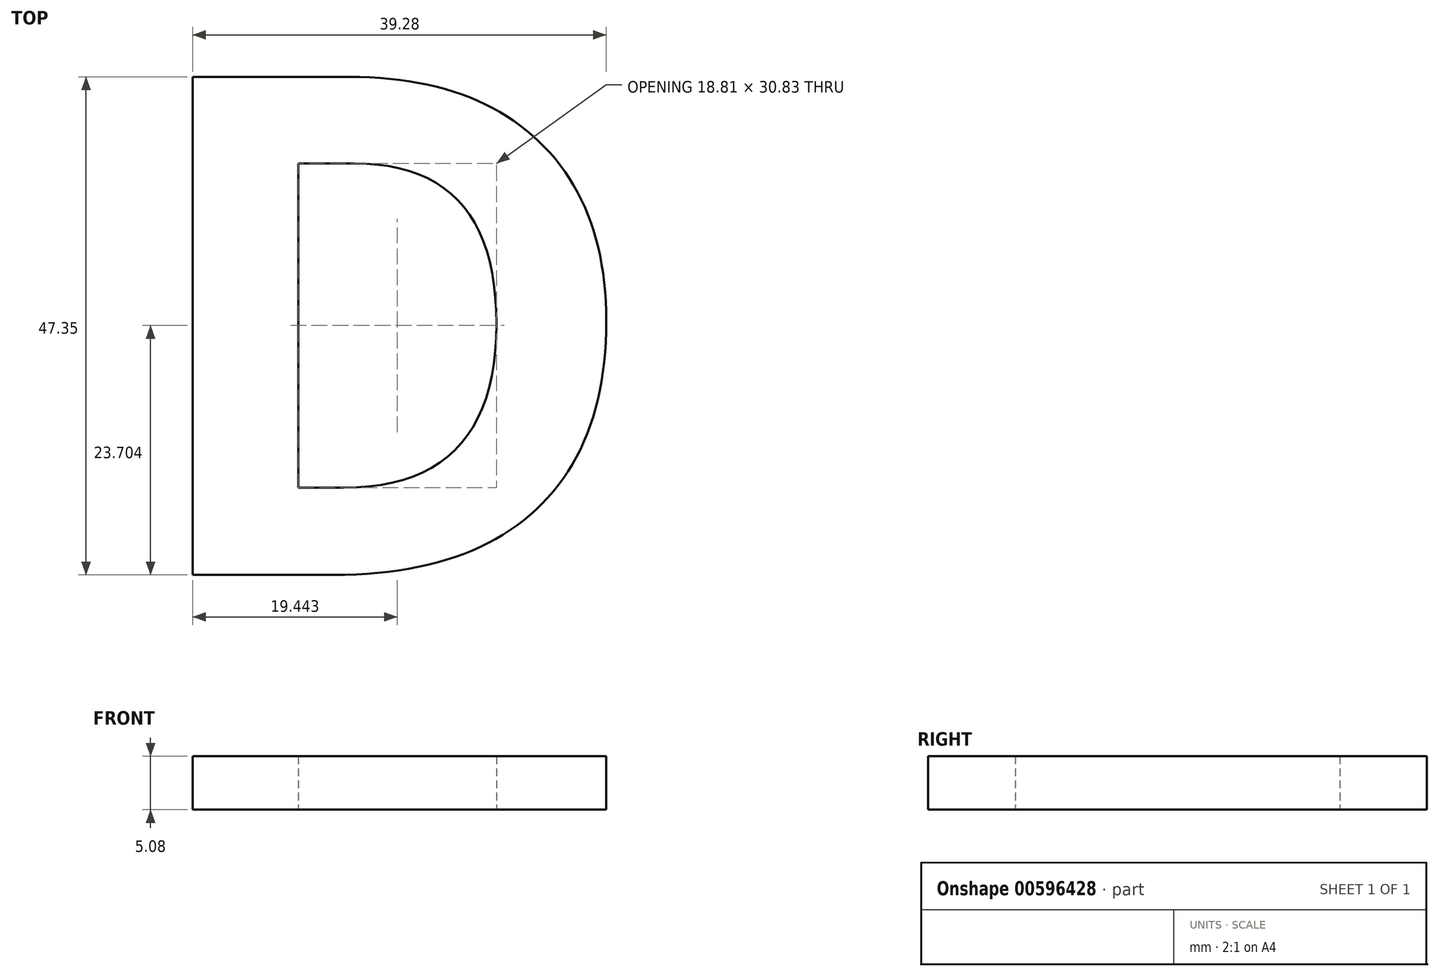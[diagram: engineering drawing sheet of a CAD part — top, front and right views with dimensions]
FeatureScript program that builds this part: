
annotation { "Feature Type Name" : "Feature", "Feature Type Description" : "" }
export const myFeature = defineFeature(function(context is Context, id is Id, definition is map)
    precondition{}
    {
        {
            var Q0;
            Q0=qCreatedBy(makeId("Top.planeOp"),FACE);
            var sketch = newSketch(context, id + "F0", { "sketchPlane" : qUnion([Q0])});
            skText(sketch, "E0", { "text": "D", "fontName": "OpenSans-Bold.ttf"});
            const initialGuessF0  = {"E0": [0, 0, 1, 0, 0.04775]};
            skSetInitialGuess(sketch, initialGuessF0);
            skSolve(sketch);
        }
        {
            var Q0;
            Q0=makeQuery(id+"F0.imprint","IMPRINT",FACE,{"disambiguationData":[TD([[makeQuery(id+"F0.imprint","IMPRINT",EDGE,{"derivedFrom":sQuery(id+"F0.wireOp",EDGE,"E0.sketch_text.stroke-0")}),-1.0]])]});
            extrude(context, id + "F1", {"entities" : qUnion([Q0]), "depth" : 5.08 * mm, "offsetDistance" : 25.4 * mm});
        }
    });
